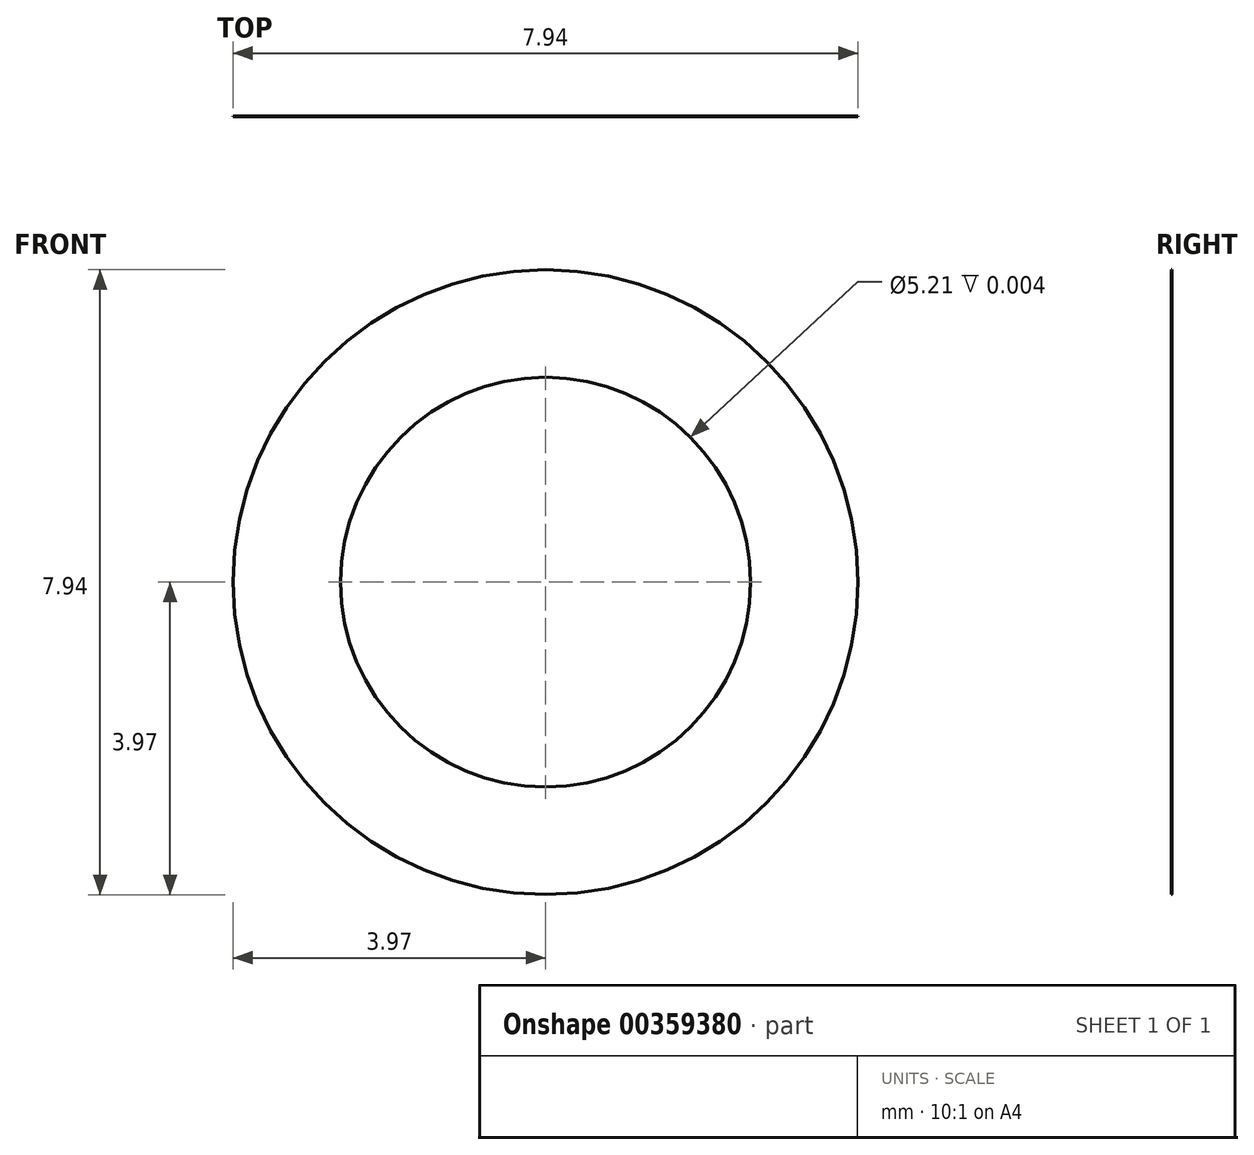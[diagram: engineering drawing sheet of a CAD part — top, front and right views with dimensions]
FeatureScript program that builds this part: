
annotation { "Feature Type Name" : "Feature", "Feature Type Description" : "" }
export const myFeature = defineFeature(function(context is Context, id is Id, definition is map)
    precondition{}
    {
        {
            var Q0;
            Q0=qCreatedBy(makeId("Front.planeOp"),FACE);
            var sketch = newSketch(context, id + "F0", { "sketchPlane" : qUnion([Q0])});
            skCircle(sketch, "E0", {"center": v(0, 0) * mm, "radius": 2.6 * mm});
            skCircle(sketch, "E1", {"center": v(0, 0) * mm, "radius": 3.97 * mm});
            skSolve(sketch);
        }
        {
            var Q0;
            Q0=makeQuery(id+"F0.imprint","IMPRINT",FACE,{"disambiguationData":[TD([[makeQuery(id+"F0.imprint","IMPRINT",EDGE,{"derivedFrom":sQuery(id+"F0.wireOp",EDGE,"E0")}),-1.0]])]});
            extrude(context, id + "F1", {"entities" : qUnion([Q0]), "depth" : 3 / 812.8 * mm});
        }
    });
